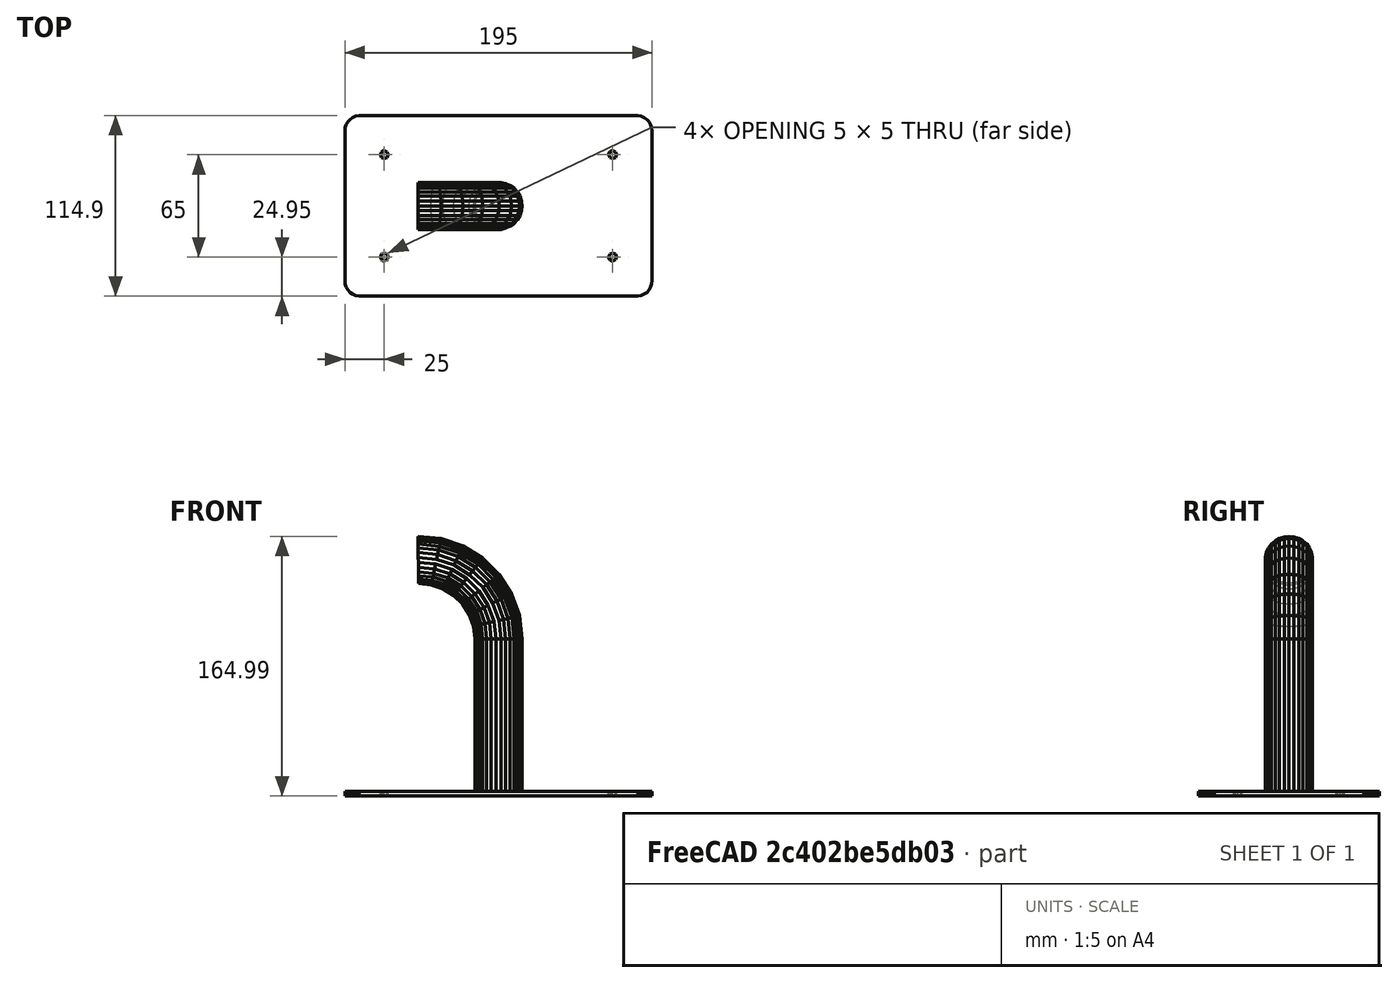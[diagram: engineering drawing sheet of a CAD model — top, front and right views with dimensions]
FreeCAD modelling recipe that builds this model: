
FCSTD DOCUMENT  (FreeCAD 0.21R33771 (Git))
Label: simple_ladder
License: All rights reserved
LicenseURL: https://en.wikipedia.org/wiki/All_rights_reserved
objects: TechDraw::DrawProjGroupItem×4, Mesh::Feature×1, Part::Feature×1, Part::Refine×1, TechDraw::DrawSVGTemplate×1, TechDraw::DrawProjGroup×1, TechDraw::DrawPage×1
note: 2 computed .brp shape members not serialized (recipe doc carries the construction recipe); baked Part::Feature solids carry a one-line shape summary decoded from their .brp

FEATURE [Mesh::Feature] simple_ladder
FEATURE [Part::Feature] simple_ladder001
  shape: bbox 195 x 114.9 x 165 mm, 872 faces, 0 solids (baked)
FEATURE [Part::Refine] simple_ladder002
  Source = -> simple_ladder001
FEATURE [TechDraw::DrawSVGTemplate] Template
  EditableTexts = Designed_by_Name=Designed by Name; Drawing_number=Drawing number; FC-Date=Date; FC-SC=Scale; FC-SH=Sheet; FC-Title=Cart Ladder; Subtitle=Subtitle; Weight=Weight
  Height = 210
  Orientation = 1
  Template = /app/share/Mod/TechDraw/Templates/A4_LandscapeTD.svg
  Width = 297
FEATURE [TechDraw::DrawProjGroupItem] ProjItem  label="Front"
  CoarseView = false
  Direction = (0,0,1)
  Focus = 100
  HardHidden = false
  IsoCount = 0
  IsoHidden = false
  IsoVisible = false
  LockPosition = true
  Perspective = false
  Rotation = 0
  RotationVector = (1,0,0)
  Scale = 0.333333
  ScaleType = 2
  ScrubCount = 0
  SeamHidden = false
  SeamVisible = false
  SmoothHidden = false
  SmoothVisible = true
  Source = -> [simple_ladder002]
  Type = 0
  X = 0
  XDirection = (1e-16,1,0)
  Y = 0
FEATURE [TechDraw::DrawProjGroupItem] ProjItem001  label="Left"
  CoarseView = false
  Direction = (-1e-16,-1,1e-16)
  Focus = 100
  HardHidden = false
  IsoCount = 0
  IsoHidden = false
  IsoVisible = false
  LockPosition = false
  Perspective = false
  Rotation = 0
  RotationVector = (1,0,0)
  ScaleType = 2
  ScrubCount = 0
  SeamHidden = false
  SeamVisible = false
  SmoothHidden = false
  SmoothVisible = true
  Source = -> [simple_ladder002]
  Type = 1
  X = 25
  XDirection = (0,1e-16,1)
  Y = 0
FEATURE [TechDraw::DrawProjGroupItem] ProjItem002  label="FrontBottomLeft"
  CoarseView = false
  Direction = (0.57735,-0.57735,0.57735)
  Focus = 100
  HardHidden = false
  IsoCount = 0
  IsoHidden = false
  IsoVisible = false
  LockPosition = false
  Perspective = false
  Rotation = 0
  RotationVector = (1,0,0)
  ScaleType = 2
  ScrubCount = 0
  SeamHidden = false
  SeamVisible = false
  SmoothHidden = false
  SmoothVisible = true
  Source = -> [simple_ladder002]
  Type = 8
  X = 25
  XDirection = (0,0.707107,0.707107)
  Y = 15
FEATURE [TechDraw::DrawProjGroupItem] ProjItem003  label="Bottom"
  CoarseView = false
  Direction = (1,-1e-16,0)
  Focus = 100
  HardHidden = false
  IsoCount = 0
  IsoHidden = false
  IsoVisible = false
  LockPosition = false
  Perspective = false
  Rotation = 0
  RotationVector = (1,0,0)
  ScaleType = 2
  ScrubCount = 0
  SeamHidden = false
  SeamVisible = false
  SmoothHidden = false
  SmoothVisible = true
  Source = -> [simple_ladder002]
  Type = 5
  X = 0
  XDirection = (1e-16,1,0)
  Y = 15
FEATURE [TechDraw::DrawProjGroup] ProjGroup
  Anchor = -> ProjItem
  AutoDistribute = true
  LockPosition = false
  ProjectionType = 0
  Rotation = 0
  Scale = 0.333333
  ScaleType = 2
  Source = -> [simple_ladder002]
  Views = -> [ProjItem,ProjItem001,ProjItem002,ProjItem003]
  X = 95.5
  Y = 88.95
  spacingX = 25
  spacingY = 15
FEATURE [TechDraw::DrawPage] Page
  KeepUpdated = true
  NextBalloonIndex = 1
  ProjectionType = 0
  Template = -> Template
  Views = -> [ProjGroup]
